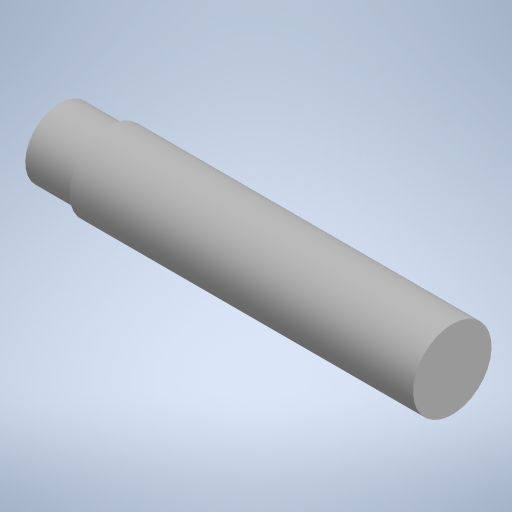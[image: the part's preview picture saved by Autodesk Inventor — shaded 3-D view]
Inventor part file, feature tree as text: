
AUTODESK INVENTOR PART (.ipt)
format: ipt  version: 2023 (Build 270158000, 158)  size: 226,816 bytes
history: native  units: mm
features: revolve x1, sketch x1
ambient origin geometry x8: Origin, YZ Plane, XZ Plane, XY Plane, X Axis, Y Axis, Z Axis, Center Point
bodies: Solid1 (feature_tree)
feature tree (2):
  revolve  "Revolution1"  [1 undecoded]
  sketch  "Sketch1"  dims[d0=6.0mm d1=5.25mm d2=7.5mm d3=60.0mm d4=90.0deg]
note: 1 required parameter value undecoded (feature->parameter linkage not recoverable at this tier; creation-order binding heuristic only, values carry confidence <= 0.55)
